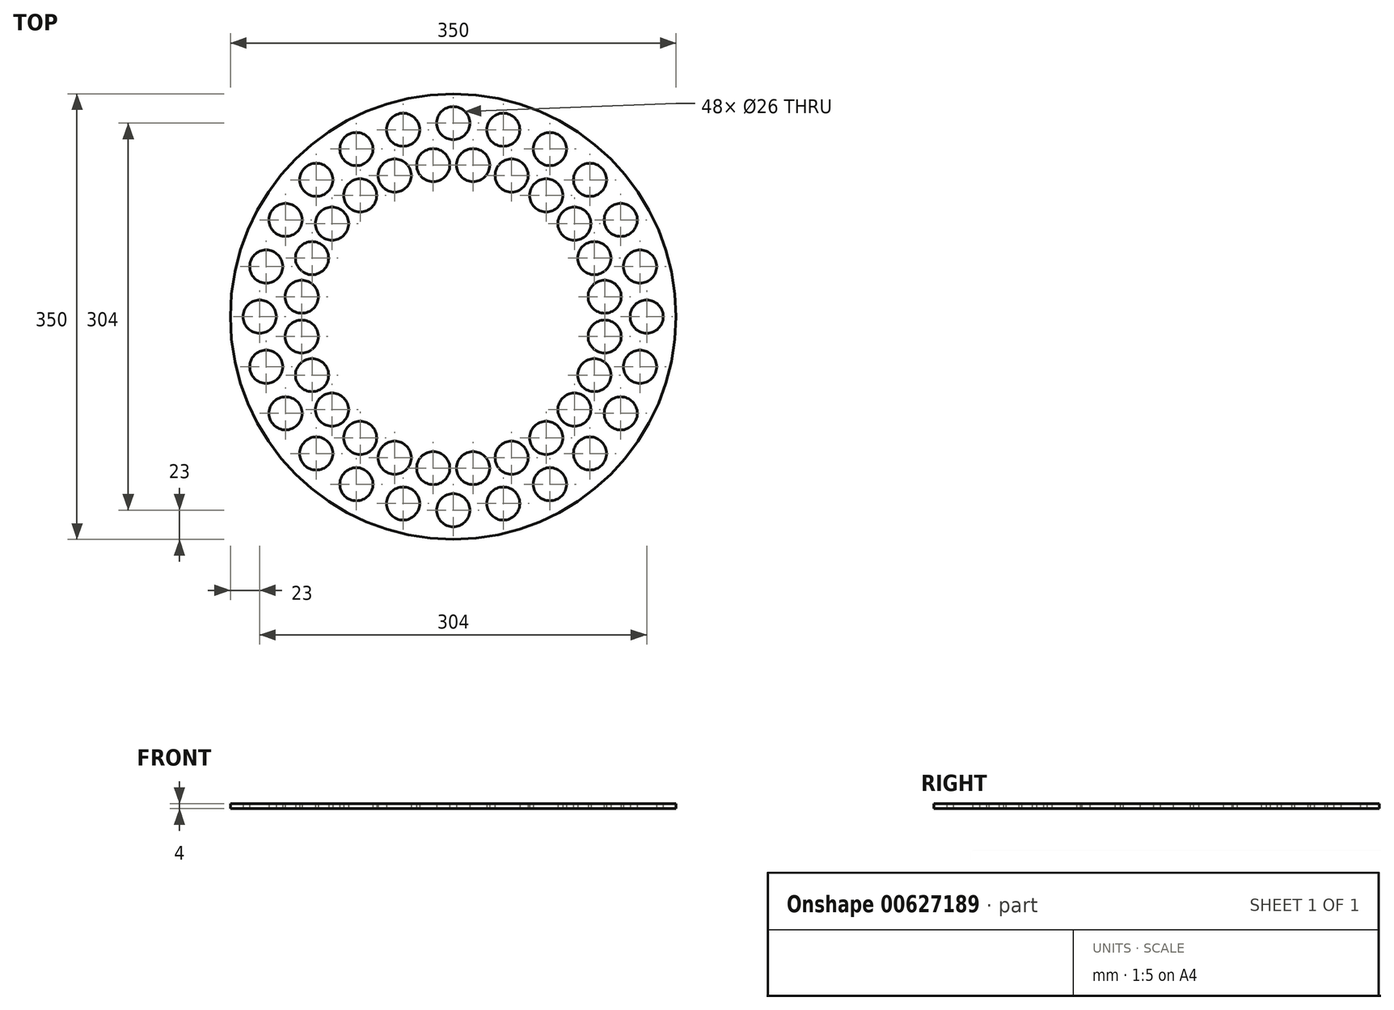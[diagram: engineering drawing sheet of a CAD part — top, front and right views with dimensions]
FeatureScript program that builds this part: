
annotation { "Feature Type Name" : "Feature", "Feature Type Description" : "" }
export const myFeature = defineFeature(function(context is Context, id is Id, definition is map)
    precondition{}
    {
        {
            var Q0;
            Q0=qCreatedBy(makeId("Top.planeOp"),FACE);
            var sketch = newSketch(context, id + "F0", { "sketchPlane" : qUnion([Q0])});
            skCircle(sketch, "E0", {"center": v(0, 0) * mm, "radius": 175 * mm});
            skLineSegment(sketch, "E1", {"start": v(0, 191.1) * mm, "end": v(0, -198.52) * mm, "construction": true});
            skLineSegment(sketch, "E2", {"start": v(-209.43, 0) * mm, "end": v(204.65, 0) * mm, "construction": true});
            skCircle(sketch, "E3", {"center": v(152, 0) * mm, "radius": 13 * mm});
            skCircle(sketch, "E4.1.0", {"center": v(146.82, 39.34) * mm, "radius": 13 * mm});
            skCircle(sketch, "E4.2.0", {"center": v(131.64, 76) * mm, "radius": 13 * mm});
            skCircle(sketch, "E4.3.0", {"center": v(107.48, 107.48) * mm, "radius": 13 * mm});
            skCircle(sketch, "E4.4.0", {"center": v(76, 131.64) * mm, "radius": 13 * mm});
            skCircle(sketch, "E4.5.0", {"center": v(39.34, 146.82) * mm, "radius": 13 * mm});
            skCircle(sketch, "E4.6.0", {"center": v(0, 152) * mm, "radius": 13 * mm});
            skCircle(sketch, "E4.7.0", {"center": v(-39.34, 146.82) * mm, "radius": 13 * mm});
            skCircle(sketch, "E4.8.0", {"center": v(-76, 131.64) * mm, "radius": 13 * mm});
            skCircle(sketch, "E4.9.0", {"center": v(-107.48, 107.48) * mm, "radius": 13 * mm});
            skCircle(sketch, "E4.10.0", {"center": v(-131.64, 76) * mm, "radius": 13 * mm});
            skCircle(sketch, "E4.11.0", {"center": v(-146.82, 39.34) * mm, "radius": 13 * mm});
            skCircle(sketch, "E4.12.0", {"center": v(-152, 0) * mm, "radius": 13 * mm});
            skCircle(sketch, "E4.13.0", {"center": v(-146.82, -39.34) * mm, "radius": 13 * mm});
            skCircle(sketch, "E4.14.0", {"center": v(-131.64, -76) * mm, "radius": 13 * mm});
            skCircle(sketch, "E4.15.0", {"center": v(-107.48, -107.48) * mm, "radius": 13 * mm});
            skCircle(sketch, "E4.16.0", {"center": v(-76, -131.64) * mm, "radius": 13 * mm});
            skCircle(sketch, "E4.17.0", {"center": v(-39.34, -146.82) * mm, "radius": 13 * mm});
            skCircle(sketch, "E4.18.0", {"center": v(0, -152) * mm, "radius": 13 * mm});
            skCircle(sketch, "E4.19.0", {"center": v(39.34, -146.82) * mm, "radius": 13 * mm});
            skCircle(sketch, "E4.20.0", {"center": v(76, -131.64) * mm, "radius": 13 * mm});
            skCircle(sketch, "E4.21.0", {"center": v(107.48, -107.48) * mm, "radius": 13 * mm});
            skCircle(sketch, "E4.22.0", {"center": v(131.64, -76) * mm, "radius": 13 * mm});
            skCircle(sketch, "E4.23.0", {"center": v(146.82, -39.34) * mm, "radius": 13 * mm});
            skLineSegment(sketch, "E5", {"start": v(0, 0) * mm, "end": v(198.29, 26.1) * mm, "construction": true});
            skCircle(sketch, "E6", {"center": v(118.97, 15.66) * mm, "radius": 13 * mm});
            skCircle(sketch, "E7.1.0", {"center": v(110.87, 45.92) * mm, "radius": 13 * mm});
            skCircle(sketch, "E7.2.0", {"center": v(95.2, 73.05) * mm, "radius": 13 * mm});
            skCircle(sketch, "E7.3.0", {"center": v(73.05, 95.2) * mm, "radius": 13 * mm});
            skCircle(sketch, "E7.4.0", {"center": v(45.92, 110.87) * mm, "radius": 13 * mm});
            skCircle(sketch, "E7.5.0", {"center": v(15.66, 118.97) * mm, "radius": 13 * mm});
            skCircle(sketch, "E7.6.0", {"center": v(-15.66, 118.97) * mm, "radius": 13 * mm});
            skCircle(sketch, "E7.7.0", {"center": v(-45.92, 110.87) * mm, "radius": 13 * mm});
            skCircle(sketch, "E7.8.0", {"center": v(-73.05, 95.2) * mm, "radius": 13 * mm});
            skCircle(sketch, "E7.9.0", {"center": v(-95.2, 73.05) * mm, "radius": 13 * mm});
            skCircle(sketch, "E7.10.0", {"center": v(-110.87, 45.92) * mm, "radius": 13 * mm});
            skCircle(sketch, "E7.11.0", {"center": v(-118.97, 15.66) * mm, "radius": 13 * mm});
            skCircle(sketch, "E7.12.0", {"center": v(-118.97, -15.66) * mm, "radius": 13 * mm});
            skCircle(sketch, "E7.13.0", {"center": v(-110.87, -45.92) * mm, "radius": 13 * mm});
            skCircle(sketch, "E7.14.0", {"center": v(-95.2, -73.05) * mm, "radius": 13 * mm});
            skCircle(sketch, "E7.15.0", {"center": v(-73.05, -95.2) * mm, "radius": 13 * mm});
            skCircle(sketch, "E7.16.0", {"center": v(-45.92, -110.87) * mm, "radius": 13 * mm});
            skCircle(sketch, "E7.17.0", {"center": v(-15.66, -118.97) * mm, "radius": 13 * mm});
            skCircle(sketch, "E7.18.0", {"center": v(15.66, -118.97) * mm, "radius": 13 * mm});
            skCircle(sketch, "E7.19.0", {"center": v(45.92, -110.87) * mm, "radius": 13 * mm});
            skCircle(sketch, "E7.20.0", {"center": v(73.05, -95.2) * mm, "radius": 13 * mm});
            skCircle(sketch, "E7.21.0", {"center": v(95.2, -73.05) * mm, "radius": 13 * mm});
            skCircle(sketch, "E7.22.0", {"center": v(110.87, -45.92) * mm, "radius": 13 * mm});
            skCircle(sketch, "E7.23.0", {"center": v(118.97, -15.66) * mm, "radius": 13 * mm});
            skSolve(sketch);
        }
        {
            var Q0;
            Q0=makeQuery(id+"F0.imprint","IMPRINT",FACE,{"disambiguationData":[TD([[makeQuery(id+"F0.imprint","IMPRINT",EDGE,{"derivedFrom":sQuery(id+"F0.wireOp",EDGE,"E0")}),1.0]])]});
            extrude(context, id + "F1", {"entities" : qUnion([Q0]), "depth" : 4 * mm, "offsetDistance" : 25 * mm});
        }
    });
